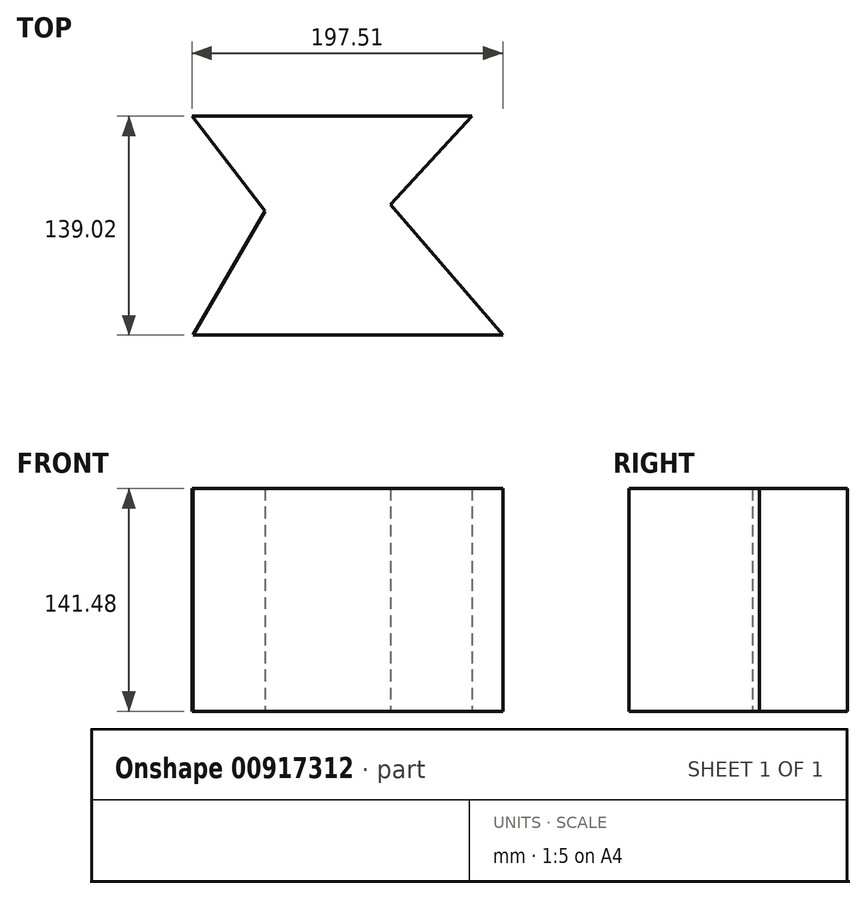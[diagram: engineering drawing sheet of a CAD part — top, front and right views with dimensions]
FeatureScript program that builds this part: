
annotation { "Feature Type Name" : "Feature", "Feature Type Description" : "" }
export const myFeature = defineFeature(function(context is Context, id is Id, definition is map)
    precondition{}
    {
        {
            var Q0;
            Q0=qCreatedBy(makeId("Top.planeOp"),FACE);
            var sketch = newSketch(context, id + "F0", { "sketchPlane" : qUnion([Q0])});
            skLineSegment(sketch, "E0", {"start": v(-94.56, 84.6) * mm, "end": v(83.24, 84.6) * mm});
            skLineSegment(sketch, "E1", {"start": v(83.24, 84.6) * mm, "end": v(31.56, 28.61) * mm});
            skLineSegment(sketch, "E2", {"start": v(31.56, 28.61) * mm, "end": v(102.95, -54.41) * mm});
            skLineSegment(sketch, "E3", {"start": v(102.95, -54.41) * mm, "end": v(-93.66, -54.41) * mm});
            skLineSegment(sketch, "E4", {"start": v(-93.66, -54.41) * mm, "end": v(-48.07, 24.23) * mm});
            skLineSegment(sketch, "E5", {"start": v(-48.07, 24.23) * mm, "end": v(-94.56, 84.6) * mm});
            skSolve(sketch);
        }
        {
            var Q0;
            Q0 = qSketchRegion(id + "F0", true);
            extrude(context, id + "F1", {"entities" : qUnion([Q0]), "depth" : 141.48 * mm, "offsetDistance" : 25.4 * mm});
        }
    });
